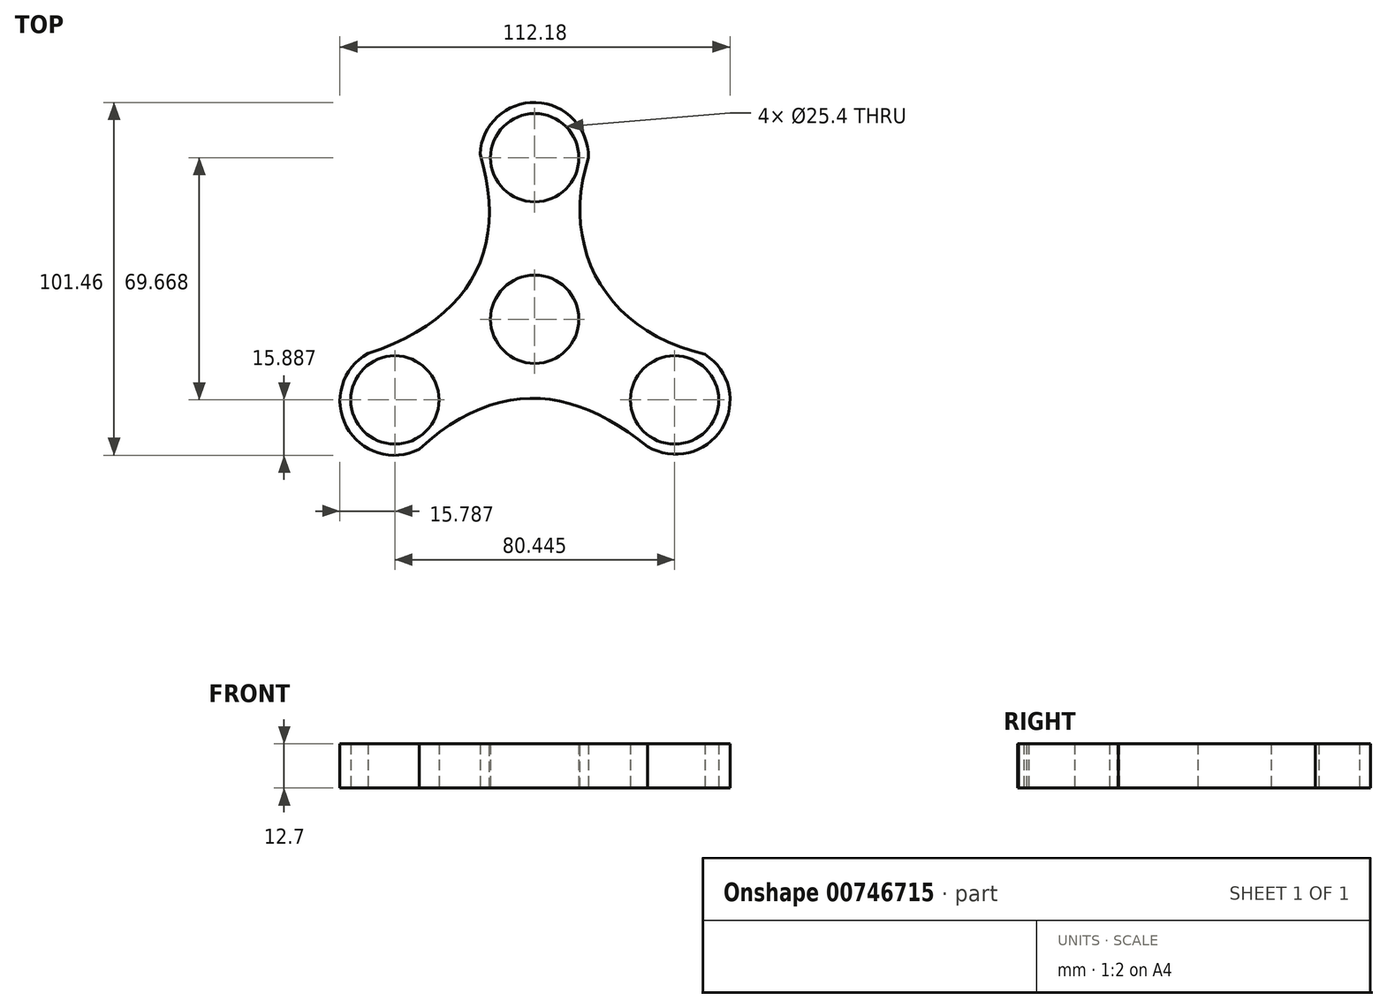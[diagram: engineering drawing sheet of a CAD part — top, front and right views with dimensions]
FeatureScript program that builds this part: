
annotation { "Feature Type Name" : "Feature", "Feature Type Description" : "" }
export const myFeature = defineFeature(function(context is Context, id is Id, definition is map)
    precondition{}
    {
        {
            var Q0;
            Q0=qCreatedBy(makeId("Top.planeOp"),FACE);
            var sketch = newSketch(context, id + "F0", { "sketchPlane" : qUnion([Q0])});
            skCircle(sketch, "E0", {"center": v(0, 0) * mm, "radius": 12.7 * mm});
            skCircle(sketch, "E1", {"center": v(0, 46.45) * mm, "radius": 12.7 * mm});
            skCircle(sketch, "E2.1.0", {"center": v(-40.22, -23.22) * mm, "radius": 12.7 * mm});
            skCircle(sketch, "E2.2.0", {"center": v(40.22, -23.22) * mm, "radius": 12.7 * mm});
            skArc(sketch, "E3", {"start": v(15.42, 46.45) * mm, "mid": v(0.36, 62.34) * mm, "end": v(-15.73, 47.49) * mm});
            skArc(sketch, "E4.1.0", {"start": v(-47.93, -9.87) * mm, "mid": v(-54.17, -30.86) * mm, "end": v(-33.26, -37.36) * mm});
            skArc(sketch, "E4.2.0", {"start": v(32.51, -36.58) * mm, "mid": v(53.8, -31.48) * mm, "end": v(48.99, -10.12) * mm});
            skFitSpline(sketch, "E5", {"points": [v(-47.93, -9.87) * mm, v(-15.73, 47.49) * mm], "startDerivative": vector(89.3, 29.6) * mm, "endDerivative": vector(-24.74, 80.99) * mm});
            skFitSpline(sketch, "E6", {"points": [v(15.42, 46.45) * mm, v(48.99, -10.12) * mm], "startDerivative": vector(-23.96, -75.12) * mm, "endDerivative": vector(88.79, -20.75) * mm});
            skFitSpline(sketch, "E7", {"points": [v(-33.26, -37.36) * mm, v(32.51, -36.58) * mm], "startDerivative": vector(68.21, 62.17) * mm, "endDerivative": vector(64.28, -51.6) * mm});
            skSolve(sketch);
        }
        {
            var Q0;
            Q0=makeQuery(id+"F0.imprint","IMPRINT",FACE,{"disambiguationData":[TD([[makeQuery(id+"F0.imprint","IMPRINT",EDGE,{"derivedFrom":sQuery(id+"F0.wireOp",EDGE,"E0")}),-1.0]])]});
            extrude(context, id + "F1", {"entities" : qUnion([Q0]), "depth" : 12.7 * mm, "offsetDistance" : 25.4 * mm});
        }
    });
